# Revit family: 2M_Strainer_UNIVAL_STR-0301 - 50-300 mm
name_source: partatom
category: Pipe Accessories
revit_build: Autodesk Revit 2016 (Build: 20150220_1215(x64)
units: mm (PartAtom-declared; Revit-internal decimal feet)

## family parameters
Always vertical = Yes
Cut with Voids When Loaded = No
OmniClass Number = 23.65.55.14
OmniClass Title = Valves for Liquid Services
Part Type = Valve - Breaks Into
Round Connector Dimension = Use Diameter
Shared = No
Work Plane-Based = No

## types (9) — shared parameters
Angle = 45.00°
Body Material = Ductile iron
Certifications = TSE, EAC, CE
Colour = UNIVAL_IRON
Connection Type = Flanged
Description = Strainer
Description TR = Pislik tutucu
Loss Method = Not Defined
Manufacturer = Giacomini Unival
Giacomini Unival
Giacomini Unival
Pressure Rating = PN25
Standard No = TS 11494
URL = http://www.unival.com.tr

## per-type parameters (varying)
| type | 1st_pipe_center_dist | 1st_pipe_dist | 1st_pipe_l | 2nd_pipe_l | Body_Do | Body_rd | DN | Flange Size | H | L | Max. Working Temperature | Model | Plate_W | Plate_d | RectangleExtr | Y_curve | Ypipe_L | Ypipe_r |
| DN125 | 25 mm  [stored 0.082021 ft] | 50 mm  [stored 0.164042 ft] | 302 mm | 130 mm | 150 mm | 75 mm | 125 mm | M_Flange - 15-450 mm : DN125 | 285 mm | 416 mm | 250°C | STR-0301X125 | 188 mm | 13 mm  [stored 0.0426509 ft] | 71 mm | 260 mm | 280 mm | 70 mm  [stored 0.229659 ft] |
| DN65 | 15 mm  [stored 0.0492126 ft] | 30 mm  [stored 0.0984252 ft] | 192 mm | 77 mm | 90 mm  [stored 0.295276 ft] | 45 mm | 65 mm | M_Flange - 15-450 mm : DN65 | 174 mm | 273 mm | 250°C | STR-0301X065 | 120 mm | 7 mm  [stored 0.0229659 ft] | 43 mm  [stored 0.141076 ft] | 120 mm | 172 mm | 42 mm |
| DN50 | 13 mm  [stored 0.0426509 ft] | 25 mm  [stored 0.082021 ft] | 144 mm | 77 mm | 75 mm | 38 mm  [stored 0.124672 ft] | 50 mm | M_Flange - 15-450 mm : DN50 | 146 mm | 230 mm | 250°C | STR-0301X050 | 100 mm  [stored 0.328084 ft] | 5 mm  [stored 0.0164042 ft] | 36 mm | 120 mm | 145 mm | 35 mm |
| DN150 | 29 mm  [stored 0.0951444 ft] | 58 mm  [stored 0.190289 ft] | 352 mm | 143 mm | 175 mm | 88 mm | 150 mm | M_Flange - 15-450 mm : DN150 | 305 mm | 470 mm | 250°C | STR-0301X150 | 225 mm | 15 mm  [stored 0.0492126 ft] | 83 mm  [stored 0.27231 ft] | 280 mm | 288 mm | 81 mm |
| DN200 | 38 mm  [stored 0.124672 ft] | 75 mm | 455 mm | 127 mm | 225 mm | 113 mm | 200 mm | M_Flange - 15-450 mm : DN200 | 401 mm | 543 mm | 250°C | STR-0301X200 | 230 mm | 20 mm  [stored 0.0656168 ft] | 107 mm | 400 mm | 382 mm | 105 mm |
| DN250 | 46 mm | 92 mm | 555 mm | 157 mm | 275 mm | 138 mm | 250 mm | M_Flange - 15-450 mm : DN250 | 473 mm | 660 mm | 250°C | STR-0301X250 | 250 mm | 25 mm  [stored 0.082021 ft] | 131 mm | 320 mm | 443 mm | 128 mm |
| DN300 | 54 mm | 108 mm  [stored 0.354331 ft] | 626 mm | 207 mm | 325 mm | 163 mm | 300 mm | M_Flange - 15-450 mm : DN300 | 554 mm | 770 mm | 250°C | STR-0301X300 | 350 mm | 30 mm  [stored 0.0984252 ft] | 155 mm | 500 mm | 517 mm | 151 mm |
| DN80 | 18 mm | 35 mm | 201 mm | 95 mm | 105 mm | 53 mm  [stored 0.173885 ft] | 80 mm | M_Flange - 15-450 mm : DN80 | 198 mm | 295 mm | 250°C | STR-0301X080 | 160 mm | 8 mm  [stored 0.0262467 ft] | 50 mm  [stored 0.164042 ft] | 150 mm | 194 mm | 49 mm |
| DN100 | 21 mm | 42 mm | 251 mm | 109 mm | 125 mm | 63 mm  [stored 0.206693 ft] | 100 mm | M_Flange - 15-450 mm : DN100 | 232 mm | 352 mm | 300°C | STR-0301X100 | 150 mm | 10 mm  [stored 0.0328084 ft] | 60 mm | 220 mm | 225 mm | 58 mm  [stored 0.190289 ft] |

note: [stored X ft] marks values corroborated as IEEE doubles in the binary element streams (Revit-internal decimal feet)

## geometry (parser evidence)
native form markers: Sweep x9
no freeform markers — native parametric forms only
